# Revit family: IN 934
name_source: partatom
category: Plumbing Fixtures
revit_build: Autodesk Revit 2017 (Build: 20160225_1515(x64)
units: mm (PartAtom-declared; Revit-internal decimal feet)

## family parameters
Always vertical = Yes
Cut with Voids When Loaded = No
OmniClass Number = 23.45.00.00
OmniClass Title = Sanitary, Laundry, and Cleaning Equipment
Part Type = Normal
Room Calculation Point = No
Round Connector Dimension = Use Diameter
Shared = No
Work Plane-Based = No

## types (1)
- IN 934
    Ca_1_Aireador Anticalcáreo = Yes
    Ca_1_Cartucho cerámico de elevada resistencia = 35 mm
    Ca_1_Caño Extensible = Yes
    Ca_1_Caño giratorio = No
    Ca_1_Incluye flexibles homologados = Yes
    Ca_1_Modelo para lavaplatos = Yes
    Ca_1_Superficie cromada de aprox = 12,5 micras.
    Ca_Alto = 386 mm
    Ca_Ancho = 192 mm
    Ca_Certificaciones = Norma UNE
    Ca_Clase de Eficiencia Energética = A+
    Ca_Creado por = Catálogo Arquitectura
    Ca_Código Catálogo Arquitectura = 412_Tek_061
    Ca_Código EAN = 8413509218449
    Ca_Código del Producto = 539341280
    Ca_Especificaciones Técnicas = Grifo de caño giratorio para cocinas modelo IN 934
    Ca_Fabricante = Teka
    Ca_Itemizado CDT = E 04 01 07
    Ca_Masterformat = 22 41 39
    Ca_Material Principal = Superficie cromada
    Ca_Producto = Grifo IN 934
    Ca_Representante = Teka
    Ca_Teléfono = 99821 1017
    Ca_Usos = Grifo para cocina
    Ca_Web del Fabricante = www.teka.cl
    Ca_Web del Representante = www.teka.cl
    Description = Grifo para cocina
    Flexible Encordado = Teka_Encordado Textil
    Grifería Teka = Teka_Niquel Cromo
    Logo Teka = Teka_Pintura Logo
    Manufacturer = Teka
    Model = IN 934
    URL = www.teka.cl

## geometry (parser evidence)
native form markers: Sweep x5
no freeform markers — native parametric forms only
